# Revit family: DuraCare-Stool-Baxter-
name_source: partatom
category: Furniture
revit_build: Autodesk Revit 2016 (Build: 20150220_1215(x64)
units: mm (PartAtom-declared; Revit-internal decimal feet)

## family parameters
Always vertical = Yes
Cut with Voids When Loaded = No
OmniClass Number = 23.40.20.00
OmniClass Title = General Furniture and Specialties
Room Calculation Point = No
Shared = No
Work Plane-Based = No

## types (2) — shared parameters
Assembly Code = E2020200
Depth = 23 3/4"
Keynote = 12500
Low Emitting Finish = Yes
Low Emitting Material = Yes
Manufacturer = DuraCare Seating
Product Documentation Link = https://duracareseating.com
Revit Model Built By = https://servex-us.com
Salvage or Reuse = Yes
Type Comments = Baxter Stool
URL = https://duracareseating.com
Width = 23"
zero-valued in all types: Percentage of Recycled Content

## per-type parameters (varying)
| type | Arm Height | Description | FR Height | H 42.5 | H 48.5 | Height | Seat Height |
| CS-249 | 31" | Counter Stool 23"W x 23.75"D x 42.5"H - aluminum frame - wood grain finish | 16" | Yes | No | 42 1/2" | 24" |
| BS-249 | 37" | Bar Stool 23"W x 23.75"D x 48.5"H - aluminum frame - wood grain finish | 18" | No | Yes | 48 1/2" | 30" |

note: column(s) folded — value = type name in every type: Model

## geometry (parser evidence)
native form markers: Sweep x8
no freeform markers — native parametric forms only
